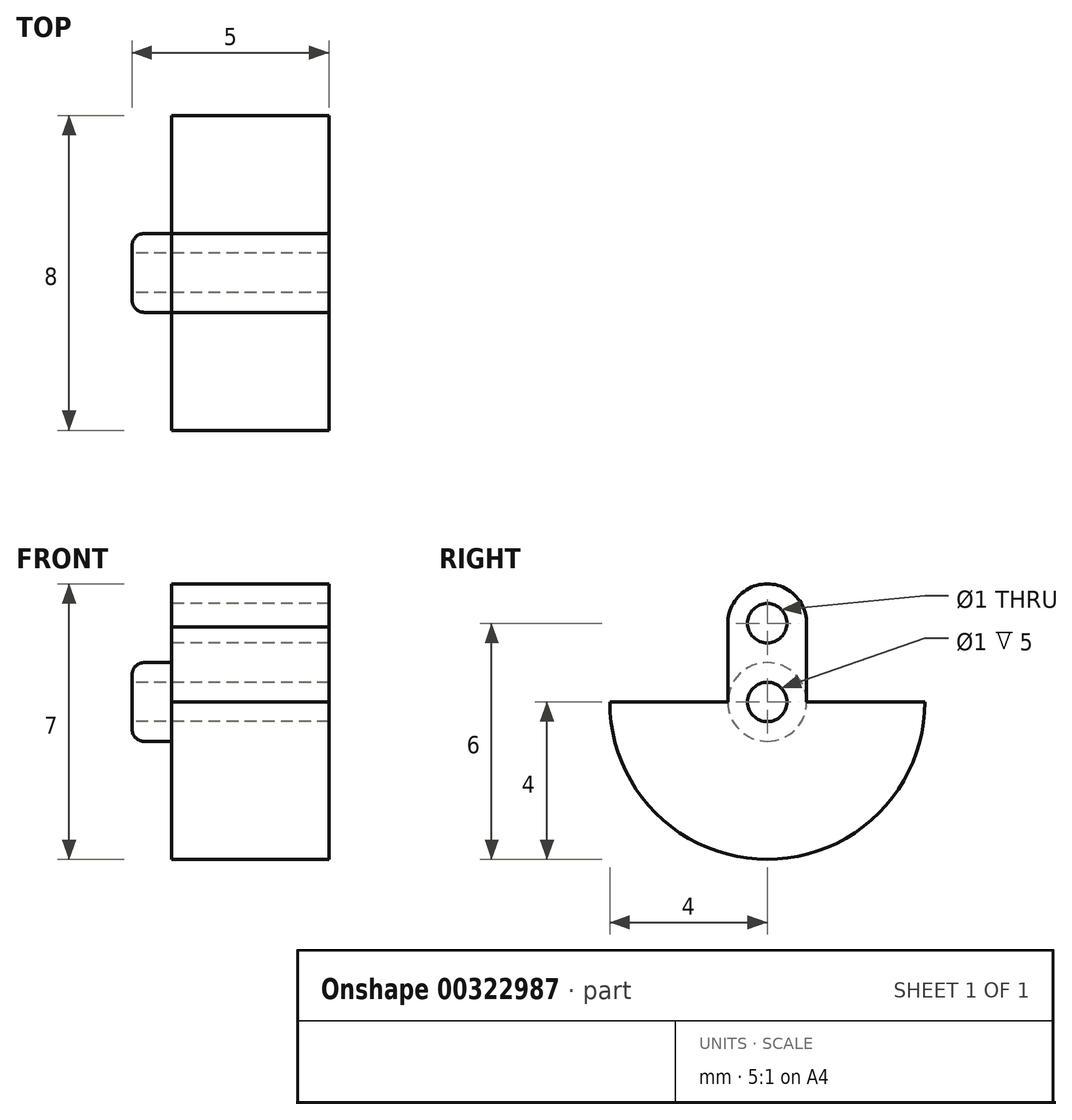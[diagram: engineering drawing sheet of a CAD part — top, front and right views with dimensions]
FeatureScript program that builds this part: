
annotation { "Feature Type Name" : "Feature", "Feature Type Description" : "" }
export const myFeature = defineFeature(function(context is Context, id is Id, definition is map)
    precondition{}
    {
        {
            var Q0;
            Q0=qCreatedBy(makeId("Front.planeOp"),FACE);
            var sketch = newSketch(context, id + "F0", { "sketchPlane" : qUnion([Q0])});
            skLineSegment(sketch, "E0", {"start": v(0, 0) * mm, "end": v(10.72, 0) * mm, "construction": true});
            skLineSegment(sketch, "E1", {"start": v(0, 0) * mm, "end": v(0, 1) * mm});
            skLineSegment(sketch, "E2", {"start": v(0, 1) * mm, "end": v(1, 1) * mm});
            skLineSegment(sketch, "E3", {"start": v(1, 1) * mm, "end": v(1, 4) * mm});
            skLineSegment(sketch, "E4", {"start": v(1, 4) * mm, "end": v(5, 4) * mm});
            skLineSegment(sketch, "E5", {"start": v(5, 4) * mm, "end": v(5, 0) * mm});
            skLineSegment(sketch, "E6", {"start": v(5, 0) * mm, "end": v(0, 0) * mm});
            skSolve(sketch);
        }
        {
            var Q0;
            Q0 = qSketchRegion(id + "F0", true);
            var Q1;
            Q1=sQuery(id+"F0.wireOp",EDGE,"E6");
            revolve(context, id + "F1", {"entities" : qUnion([Q0]), "axis" : qUnion([Q1]), "revolveType" : RevolveType.FULL});
        }
        {
            var Q0;
            Q0=qCreatedBy(makeId("Right.planeOp"),FACE);
            var sketch = newSketch(context, id + "F2", { "sketchPlane" : qUnion([Q0])});
            skCircle(sketch, "E7", {"center": v(0, 0) * mm, "radius": 0.5 * mm});
            skCircle(sketch, "E8", {"center": v(0, 2) * mm, "radius": 0.5 * mm});
            skCircle(sketch, "E9", {"center": v(0, 2) * mm, "radius": 1 * mm, "construction": true});
            skLineSegment(sketch, "E10", {"start": v(0, 0) * mm, "end": v(1, 0) * mm, "construction": true});
            skLineSegment(sketch, "E11.MirrorCS", {"start": v(0, 0) * mm, "end": v(-1, 0) * mm, "construction": true});
            skLineSegment(sketch, "E12", {"start": v(1, 0) * mm, "end": v(1, 1.9) * mm});
            skLineSegment(sketch, "E13", {"start": v(1, 0) * mm, "end": v(4, 0) * mm});
            skLineSegment(sketch, "E14.MirrorCS", {"start": v(-1, 0) * mm, "end": v(-1, 1.9) * mm});
            skLineSegment(sketch, "E15.MirrorCS", {"start": v(-1, 0) * mm, "end": v(-4, 0) * mm});
            skArc(sketch, "E16", {"start": v(1, 1.9) * mm, "mid": v(0, 3) * mm, "end": v(-1, 1.9) * mm});
            skArc(sketch, "E17", {"start": v(4, 0) * mm, "mid": v(0, -4) * mm, "end": v(-4, 0) * mm});
            skSolve(sketch);
        }
        {
            var Q0;
            Q0=makeQuery(id+"F2.imprint","IMPRINT",FACE,{"disambiguationData":[TD([[makeQuery(id+"F2.imprint","IMPRINT",EDGE,{"derivedFrom":sQuery(id+"F2.wireOp",EDGE,"E7")}),-1.0]])]});
            extrude(context, id + "F3", {"entities" : qUnion([Q0]), "operationType" : NewBodyOperationType.INTERSECT, "depth" : 25 * mm});
        }
        {
            var Q0;
            Q0=makeQuery(id+"F3.boolean.opBoolean","COPY",EDGE,{"derivedFrom":makeQuery(id+"F3.boolean.toolComplement.opBoolean","COPY",EDGE,{"derivedFrom":makeQuery(id+"F3.opExtrude","SWEPT_EDGE",EDGE,{"disambiguationData":[OSD([sQuery(id+"F2.wireOp",EDGE,"E15.MirrorCS"),sQuery(id+"F2.wireOp",EDGE,"E17")])]})})});
            var Q1;
            Q1=makeQuery(id+"F3.boolean.opBoolean","COPY",EDGE,{"derivedFrom":makeQuery(id+"F3.boolean.toolComplement.opBoolean","COPY",EDGE,{"derivedFrom":makeQuery(id+"F3.opExtrude","SWEPT_EDGE",EDGE,{"disambiguationData":[OSD([sQuery(id+"F2.wireOp",EDGE,"E13"),sQuery(id+"F2.wireOp",EDGE,"E17")])]})})});
            var Q2;
            Q2=makeQuery(id+"F1.opRevolve","SWEPT_EDGE",EDGE,{"disambiguationData":[OSD([sQuery(id+"F0.wireOp",EDGE,"E1"),sQuery(id+"F0.wireOp",EDGE,"E2")])]});
            fillet(context, id + "F4", {"entities" : qUnion([Q0, Q1, Q2]), "radius" : 0.3 * mm, "tangentPropagation" : true, "allowEdgeOverflow" : false});
        }
    });
